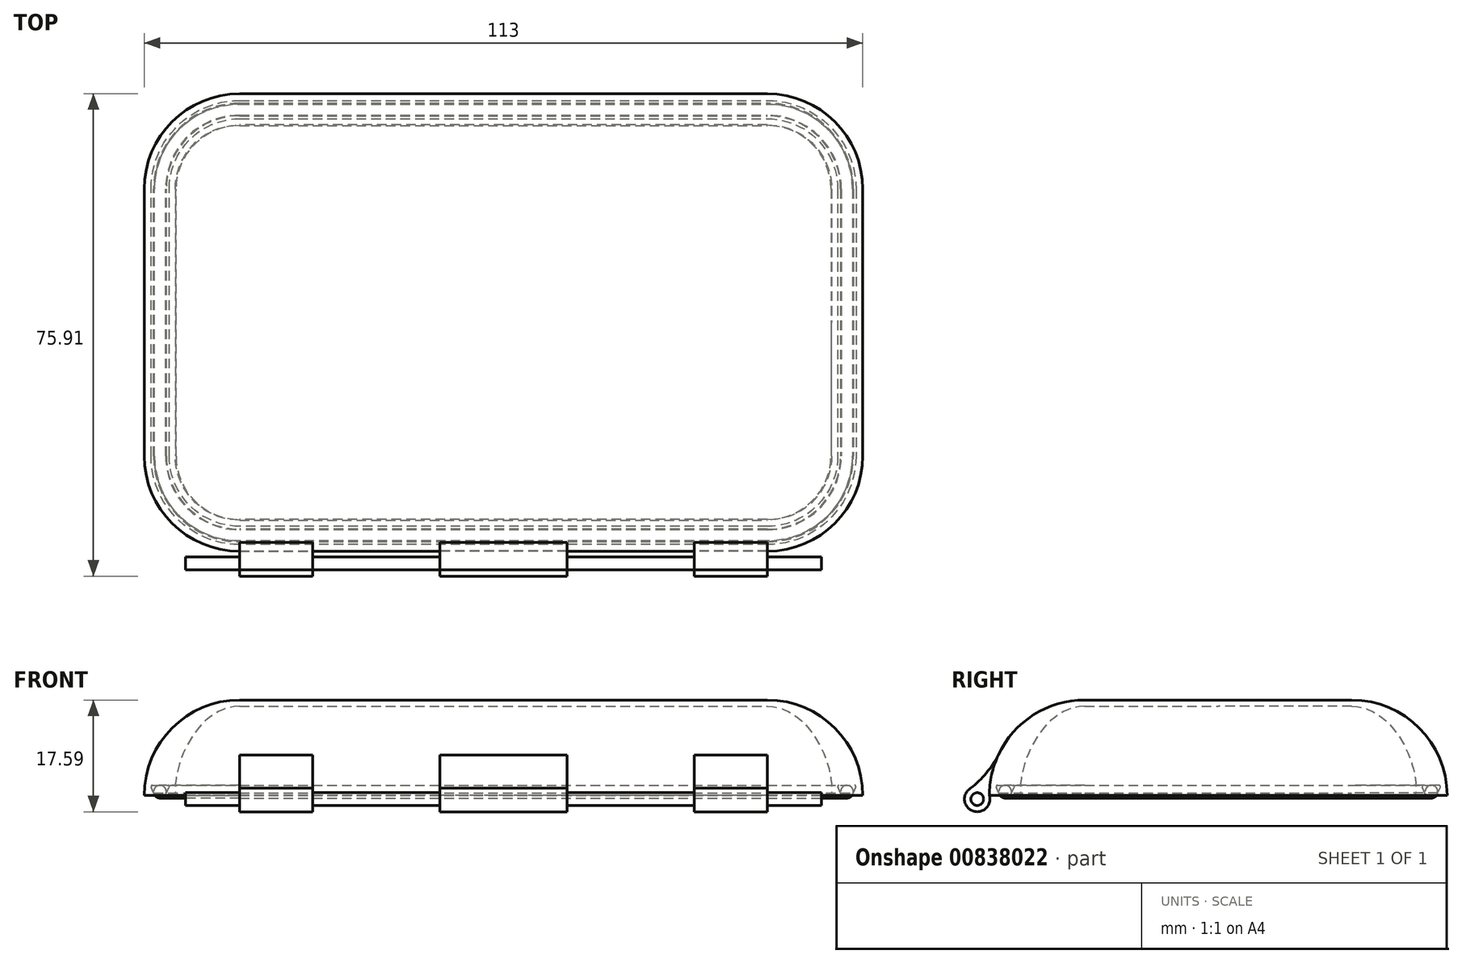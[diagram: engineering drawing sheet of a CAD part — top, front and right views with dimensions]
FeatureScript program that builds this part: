
annotation { "Feature Type Name" : "Feature", "Feature Type Description" : "" }
export const myFeature = defineFeature(function(context is Context, id is Id, definition is map)
    precondition{}
    {
        {
            var Q0;
            Q0=qCreatedBy(makeId("Top.planeOp"),FACE);
            var sketch = newSketch(context, id + "F0", { "sketchPlane" : qUnion([Q0])});
            skLineSegment(sketch, "E0", {"start": v(0, 0) * mm, "end": v(0, 27) * mm, "construction": true});
            skLineSegment(sketch, "E1", {"start": v(0, 27) * mm, "end": v(41.5, 27) * mm});
            skLineSegment(sketch, "E2", {"start": v(47.5, 21) * mm, "end": v(47.5, 0) * mm});
            skLineSegment(sketch, "E3", {"start": v(47.5, 0) * mm, "end": v(0, 0) * mm, "construction": true});
            skLineSegment(sketch, "E4.MirrorCS", {"start": v(0, 27) * mm, "end": v(-41.5, 27) * mm});
            skLineSegment(sketch, "E5.MirrorCS", {"start": v(-47.5, 21) * mm, "end": v(-47.5, 0) * mm});
            skLineSegment(sketch, "E6.MirrorCS", {"start": v(0, -27) * mm, "end": v(-41.5, -27) * mm});
            skLineSegment(sketch, "E7.MirrorCS", {"start": v(0, -27) * mm, "end": v(41.5, -27) * mm});
            skLineSegment(sketch, "E8.MirrorCS", {"start": v(47.5, -21) * mm, "end": v(47.5, 0) * mm});
            skLineSegment(sketch, "E9.MirrorCS", {"start": v(-47.5, -21) * mm, "end": v(-47.5, 0) * mm});
            skPoint(sketch, "E10.visualSharp", {"position": v(47.5, 27) * mm});
            skArc(sketch, "E10.filletArc", {"start": v(47.5, 21) * mm, "mid": v(45.74, 25.24) * mm, "end": v(41.5, 27) * mm});
            skPoint(sketch, "E11.visualSharp", {"position": v(-47.5, 27) * mm});
            skArc(sketch, "E11.filletArc", {"start": v(-41.5, 27) * mm, "mid": v(-45.74, 25.24) * mm, "end": v(-47.5, 21) * mm});
            skPoint(sketch, "E12.visualSharp", {"position": v(-47.5, -27) * mm});
            skArc(sketch, "E12.filletArc", {"start": v(-47.5, -21) * mm, "mid": v(-45.74, -25.24) * mm, "end": v(-41.5, -27) * mm});
            skPoint(sketch, "E13.visualSharp", {"position": v(47.5, -27) * mm});
            skArc(sketch, "E13.filletArc", {"start": v(41.5, -27) * mm, "mid": v(45.74, -25.24) * mm, "end": v(47.5, -21) * mm});
            skLineSegment(sketch, "E14.0", {"start": v(0, 31) * mm, "end": v(-41.5, 31) * mm});
            skArc(sketch, "E14.1", {"start": v(41.5, -31) * mm, "mid": v(48.57, -28.07) * mm, "end": v(51.5, -21) * mm});
            skLineSegment(sketch, "E14.2", {"start": v(51.5, -21) * mm, "end": v(51.5, 0) * mm});
            skLineSegment(sketch, "E14.3", {"start": v(51.5, 21) * mm, "end": v(51.5, 0) * mm});
            skArc(sketch, "E14.4", {"start": v(51.5, 21) * mm, "mid": v(48.57, 28.07) * mm, "end": v(41.5, 31) * mm});
            skLineSegment(sketch, "E14.5", {"start": v(0, -31) * mm, "end": v(41.5, -31) * mm});
            skLineSegment(sketch, "E14.6", {"start": v(0, 31) * mm, "end": v(41.5, 31) * mm});
            skLineSegment(sketch, "E14.7", {"start": v(0, -31) * mm, "end": v(-41.5, -31) * mm});
            skArc(sketch, "E14.8", {"start": v(-51.5, -21) * mm, "mid": v(-48.57, -28.07) * mm, "end": v(-41.5, -31) * mm});
            skLineSegment(sketch, "E14.9", {"start": v(-51.5, -21) * mm, "end": v(-51.5, 0) * mm});
            skLineSegment(sketch, "E14.10", {"start": v(-51.5, 21) * mm, "end": v(-51.5, 0) * mm});
            skArc(sketch, "E14.11", {"start": v(-41.5, 31) * mm, "mid": v(-48.57, 28.07) * mm, "end": v(-51.5, 21) * mm});
            skLineSegment(sketch, "E15", {"start": v(41.5, -21) * mm, "end": v(41.5, 21) * mm});
            skLineSegment(sketch, "E16", {"start": v(41.5, 21) * mm, "end": v(-41.5, 21) * mm});
            skLineSegment(sketch, "E17", {"start": v(-41.5, 21) * mm, "end": v(-41.5, -21) * mm});
            skLineSegment(sketch, "E18", {"start": v(-41.5, -21) * mm, "end": v(41.5, -21) * mm});
            skLineSegment(sketch, "E19", {"start": v(-41.5, -21) * mm, "end": v(-48.57, -28.07) * mm, "construction": true});
            skCircle(sketch, "E20", {"center": v(-47.5, -27) * mm, "radius": 2.5 * mm});
            skSolve(sketch);
        }
        {
            var Q0;
            Q0=qCreatedBy(makeId("Front.planeOp"),FACE);
            var sketch = newSketch(context, id + "F1", { "sketchPlane" : qUnion([Q0])});
            skArc(sketch, "E21", {"start": v(56.5, 0) * mm, "mid": v(52.1, 10.6) * mm, "end": v(41.5, 15) * mm});
            skFitSpline(sketch, "E22", {"points": [v(41.5, 14) * mm, v(51.5, 0) * mm, v(41.5, -12.07) * mm], "startDerivative": vector(40.14, 0) * mm, "endDerivative": vector(-25.73, -56.42) * mm});
            skLineSegment(sketch, "E23", {"start": v(41.5, 15) * mm, "end": v(41.5, 14) * mm});
            skLineSegment(sketch, "E24", {"start": v(41.5, 14) * mm, "end": v(41.5, 0) * mm, "construction": true});
            skCircle(sketch, "E25", {"center": v(54.02, 0.56) * mm, "radius": 1 * mm});
            skLineSegment(sketch, "E26", {"start": v(53.11, 0.14) * mm, "end": v(52.58, 1.28) * mm});
            skLineSegment(sketch, "E27", {"start": v(52.76, 1.56) * mm, "end": v(54, 1.56) * mm});
            skArc(sketch, "E28.filletArc", {"start": v(52.76, 1.56) * mm, "mid": v(52.6, 1.47) * mm, "end": v(52.58, 1.28) * mm});
            skLineSegment(sketch, "E29", {"start": v(53.02, 0) * mm, "end": v(51.5, 0) * mm});
            skArc(sketch, "E30.filletArc", {"start": v(53.02, 0) * mm, "mid": v(53.1, 0.05) * mm, "end": v(53.11, 0.14) * mm});
            skLineSegment(sketch, "E31", {"start": v(54, 1.56) * mm, "end": v(54, 2.15) * mm, "construction": true});
            skLineSegment(sketch, "E32.MirrorCS", {"start": v(55.24, 1.56) * mm, "end": v(54, 1.56) * mm});
            skArc(sketch, "E33.MirrorCS", {"start": v(55.24, 1.56) * mm, "mid": v(55.4, 1.47) * mm, "end": v(55.42, 1.28) * mm});
            skLineSegment(sketch, "E34.MirrorCS", {"start": v(54.89, 0.14) * mm, "end": v(55.42, 1.28) * mm});
            skArc(sketch, "E35.MirrorCS", {"start": v(54.98, 0) * mm, "mid": v(54.9, 0.05) * mm, "end": v(54.89, 0.14) * mm});
            skLineSegment(sketch, "E36.MirrorCS", {"start": v(54.98, 0) * mm, "end": v(56.5, 0) * mm});
            skSolve(sketch);
        }
        {
            var Q0;
            Q0=makeQuery(id+"F1.imprint","IMPRINT",FACE,{"disambiguationData":[TD([[makeQuery(id+"F1.imprint","IMPRINT",EDGE,{"derivedFrom":sQuery(id+"F1.wireOp",EDGE,"E21")}),1.0]])]});
            var Q1;
            {var subQ3=sQuery(id+"F1.wireOp",EDGE,"E25");var subQ7=makeQuery(id+"F1.imprint","INTERSECT",VERTEX,{"derivedFrom":[subQ3,sQuery(id+"F1.wireOp",EDGE,"E32.MirrorCS")]});Q1=makeQuery(id+"F1.imprint","IMPRINT",FACE,{"disambiguationData":[TD([[makeQuery(id+"F1.imprint","IMPRINT",EDGE,{"disambiguationData":[TD([[subQ7,1.0]])],"derivedFrom":subQ3}),1.0]])]});}
            var Q2;
            Q2=sQuery(id+"F0.wireOp",EDGE,"E14.2");
            var Q3;
            Q3=sQuery(id+"F0.wireOp",EDGE,"E14.1");
            var Q4;
            Q4=sQuery(id+"F0.wireOp",EDGE,"E14.5");
            var Q5;
            Q5=sQuery(id+"F0.wireOp",EDGE,"E14.7");
            var Q6;
            Q6=sQuery(id+"F0.wireOp",EDGE,"E14.8");
            var Q7;
            Q7=sQuery(id+"F0.wireOp",EDGE,"E14.9");
            var Q8;
            Q8=sQuery(id+"F0.wireOp",EDGE,"E14.10");
            var Q9;
            Q9=sQuery(id+"F0.wireOp",EDGE,"E14.11");
            var Q10;
            Q10=sQuery(id+"F0.wireOp",EDGE,"E14.0");
            var Q11;
            Q11=sQuery(id+"F0.wireOp",EDGE,"E14.6");
            var Q12;
            Q12=sQuery(id+"F0.wireOp",EDGE,"E14.4");
            var Q13;
            Q13=sQuery(id+"F0.wireOp",EDGE,"E14.3");
            sweep(context, id + "F2", {"profiles" : qUnion([Q0, Q1]), "path" : qUnion([Q2, Q3, Q4, Q5, Q6, Q7, Q8, Q9, Q10, Q11, Q12, Q13])});
        }
        {
            var Q0;
            Q0=makeQuery(id+"F0.imprint","IMPRINT",FACE,{"disambiguationData":[TD([[makeQuery(id+"F0.imprint","IMPRINT",EDGE,{"derivedFrom":sQuery(id+"F0.wireOp",EDGE,"E15")}),1.0]])]});
            extrude(context, id + "F3", {"entities" : qUnion([Q0]), "operationType" : NewBodyOperationType.ADD, "depth" : 15 * mm, "offsetDistance" : 25 * mm, "hasSecondDirection" : true, "secondDirectionOppositeDirection" : false, "secondDirectionDepth" : 14 * mm});
        }
        {
            var Q0;
            Q0=makeQuery(id+"F3.boolean.opBoolean","MERGE",VERTEX,{"derivedFrom":[makeQuery(id+"F2.opSweep","MID_CAP_VERTEX",VERTEX,{"disambiguationData":[OSD([sQuery(id+"F0.wireOp",EDGE,"E14.0"),sQuery(id+"F1.wireOp",EDGE,"E21"),sQuery(id+"F1.wireOp",EDGE,"E23")])],"capPos":8.0}),makeQuery(id+"F3.opExtrude","CAP_VERTEX",VERTEX,{"disambiguationData":[OSD([sQuery(id+"F0.wireOp",EDGE,"E16"),sQuery(id+"F0.wireOp",EDGE,"E17")])],"isStart":false})]});
            var Q1;
            Q1=makeQuery(id+"F3.boolean.opBoolean","MERGE",VERTEX,{"derivedFrom":[makeQuery(id+"F2.opSweep","MID_CAP_VERTEX",VERTEX,{"disambiguationData":[OSD([sQuery(id+"F0.wireOp",EDGE,"E14.9"),sQuery(id+"F1.wireOp",EDGE,"E21"),sQuery(id+"F1.wireOp",EDGE,"E23")])],"capPos":5.0}),makeQuery(id+"F3.opExtrude","CAP_VERTEX",VERTEX,{"disambiguationData":[OSD([sQuery(id+"F0.wireOp",EDGE,"E17"),sQuery(id+"F0.wireOp",EDGE,"E18")])],"isStart":false})]});
            var Q2;
            Q2=makeQuery(id+"F2.opSweep","MID_CAP_VERTEX",VERTEX,{"disambiguationData":[OSD([sQuery(id+"F0.wireOp",EDGE,"E14.8"),sQuery(id+"F1.wireOp",EDGE,"E21"),sQuery(id+"F1.wireOp",EDGE,"E36.MirrorCS")])],"capPos":4.0});
            cPlane(context, id + "F4", {"entities" : qUnion([Q0, Q1, Q2]), "cplaneType" : CPlaneType.THREE_POINT, "offset" : 0 * mm, "width" : 150 * mm, "height" : 150 * mm});
        }
        {
            var Q0;
            Q0=makeQuery(id+"F3.boolean.opBoolean","MERGE",VERTEX,{"derivedFrom":[makeQuery(id+"F2.opSweep","MID_CAP_VERTEX",VERTEX,{"disambiguationData":[OSD([sQuery(id+"F0.wireOp",EDGE,"E14.5"),sQuery(id+"F1.wireOp",EDGE,"E21"),sQuery(id+"F1.wireOp",EDGE,"E23")])],"capPos":2.0}),makeQuery(id+"F3.opExtrude","CAP_VERTEX",VERTEX,{"disambiguationData":[OSD([sQuery(id+"F0.wireOp",EDGE,"E15"),sQuery(id+"F0.wireOp",EDGE,"E18")])],"isStart":false})]});
            var Q1;
            Q1=makeQuery(id+"F3.boolean.opBoolean","MERGE",VERTEX,{"derivedFrom":[makeQuery(id+"F2.opSweep","MID_CAP_VERTEX",VERTEX,{"disambiguationData":[OSD([sQuery(id+"F0.wireOp",EDGE,"E14.3"),sQuery(id+"F1.wireOp",EDGE,"E21"),sQuery(id+"F1.wireOp",EDGE,"E23")])],"capPos":11.0}),makeQuery(id+"F3.opExtrude","CAP_VERTEX",VERTEX,{"disambiguationData":[OSD([sQuery(id+"F0.wireOp",EDGE,"E15"),sQuery(id+"F0.wireOp",EDGE,"E16")])],"isStart":false})]});
            var Q2;
            Q2=makeQuery(id+"F2.opSweep","MID_CAP_VERTEX",VERTEX,{"disambiguationData":[OSD([sQuery(id+"F0.wireOp",EDGE,"E14.4"),sQuery(id+"F1.wireOp",EDGE,"E21"),sQuery(id+"F1.wireOp",EDGE,"E36.MirrorCS")])],"capPos":10.0});
            cPlane(context, id + "F5", {"entities" : qUnion([Q0, Q1, Q2]), "cplaneType" : CPlaneType.THREE_POINT, "offset" : 25 * mm, "width" : 150 * mm, "height" : 150 * mm});
        }
        {
            var Q0;
            Q0=qCreatedBy(makeId("Right.planeOp"),FACE);
            var sketch = newSketch(context, id + "F6", { "sketchPlane" : qUnion([Q0])});
            skPoint(sketch, "E37", {"position": v(-21, 15) * mm});
            skPoint(sketch, "E38", {"position": v(-36, 0) * mm});
            skLineSegment(sketch, "E39", {"start": v(-21, 15) * mm, "end": v(-21, 0) * mm, "construction": true});
            skLineSegment(sketch, "E40", {"start": v(-36, 0) * mm, "end": v(-21, 0) * mm, "construction": true});
            skArc(sketch, "E41", {"start": v(-21, 15) * mm, "mid": v(-31.6, 10.6) * mm, "end": v(-36, 0) * mm});
            skLineSegment(sketch, "E42", {"start": v(-21, 0) * mm, "end": v(-40.9, -0.7) * mm, "construction": true});
            skCircle(sketch, "E43", {"center": v(-37.91, -0.6) * mm, "radius": 2 * mm});
            skArc(sketch, "E44", {"start": v(-38.95, 1.12) * mm, "mid": v(-36.48, 3.5) * mm, "end": v(-34.59, 6.35) * mm});
            skPoint(sketch, "E45", {"position": v(-34.59, 6.35) * mm});
            skCircle(sketch, "E46", {"center": v(-37.91, -0.6) * mm, "radius": 1 * mm});
            skSolve(sketch);
        }
        {
            var Q0;
            Q0 = qSketchRegion(id + "F6", true);
            extrude(context, id + "F7", {"entities" : qUnion([Q0]), "operationType" : NewBodyOperationType.ADD, "depth" : 20 * mm, "offsetDistance" : 25 * mm, "symmetric" : true});
        }
        {
            var Q0;
            {var subQ3=sQuery(id+"F6.wireOp",EDGE,"E44");Q0=makeQuery(id+"F6.imprint","IMPRINT",FACE,{"disambiguationData":[TD([[makeQuery(id+"F6.imprint","IMPRINT",EDGE,{"derivedFrom":subQ3}),-1.0]])]});}
            var Q1;
            {var subQ0=sQuery(id+"F6.wireOp",EDGE,"E43");var subQ1=makeQuery(id+"F6.imprint","INTERSECT",VERTEX,{"derivedFrom":[sQuery(id+"F6.wireOp",EDGE,"E41"),subQ0]});Q1=makeQuery(id+"F6.imprint","IMPRINT",FACE,{"disambiguationData":[TD([[makeQuery(id+"F6.imprint","IMPRINT",EDGE,{"disambiguationData":[TD([[subQ1,-1.0]])],"derivedFrom":subQ0}),1.0]])]});}
            var Q2;
            Q2=qCreatedBy(id+"F4.planeOp",FACE);
            extrude(context, id + "F8", {"entities" : qUnion([Q0, Q1]), "operationType" : NewBodyOperationType.ADD, "endBound" : BoundingType.UP_TO_SURFACE, "oppositeDirection" : true, "depth" : 25 * mm, "endBoundEntityFace" : qUnion([Q2]), "offsetDistance" : 25 * mm, "hasSecondDirection" : true, "secondDirectionOppositeDirection" : true, "secondDirectionDepth" : 30 * mm});
        }
        {
            var Q0;
            {var subQ3=sQuery(id+"F6.wireOp",EDGE,"E44");Q0=makeQuery(id+"F6.imprint","IMPRINT",FACE,{"disambiguationData":[TD([[makeQuery(id+"F6.imprint","IMPRINT",EDGE,{"derivedFrom":subQ3}),-1.0]])]});}
            var Q1;
            {var subQ0=sQuery(id+"F6.wireOp",EDGE,"E43");var subQ1=makeQuery(id+"F6.imprint","INTERSECT",VERTEX,{"derivedFrom":[sQuery(id+"F6.wireOp",EDGE,"E41"),subQ0]});Q1=makeQuery(id+"F6.imprint","IMPRINT",FACE,{"disambiguationData":[TD([[makeQuery(id+"F6.imprint","IMPRINT",EDGE,{"disambiguationData":[TD([[subQ1,-1.0]])],"derivedFrom":subQ0}),1.0]])]});}
            var Q2;
            Q2=qCreatedBy(id+"F5.planeOp",FACE);
            extrude(context, id + "F9", {"entities" : qUnion([Q0, Q1]), "operationType" : NewBodyOperationType.ADD, "endBound" : BoundingType.UP_TO_SURFACE, "depth" : 50 * mm, "endBoundEntityFace" : qUnion([Q2]), "offsetDistance" : 25 * mm, "hasSecondDirection" : true, "secondDirectionOppositeDirection" : false, "secondDirectionDepth" : 30 * mm});
        }
        {
            var Q0;
            Q0=makeQuery(id+"F6.imprint","IMPRINT",FACE,{"disambiguationData":[TD([[makeQuery(id+"F6.imprint","IMPRINT",EDGE,{"derivedFrom":sQuery(id+"F6.wireOp",EDGE,"E46")}),1.0]])]});
            extrude(context, id + "F10", {"entities" : qUnion([Q0]), "operationType" : NewBodyOperationType.ADD, "depth" : 100 * mm, "offsetDistance" : 25 * mm, "symmetric" : true});
        }
    });
